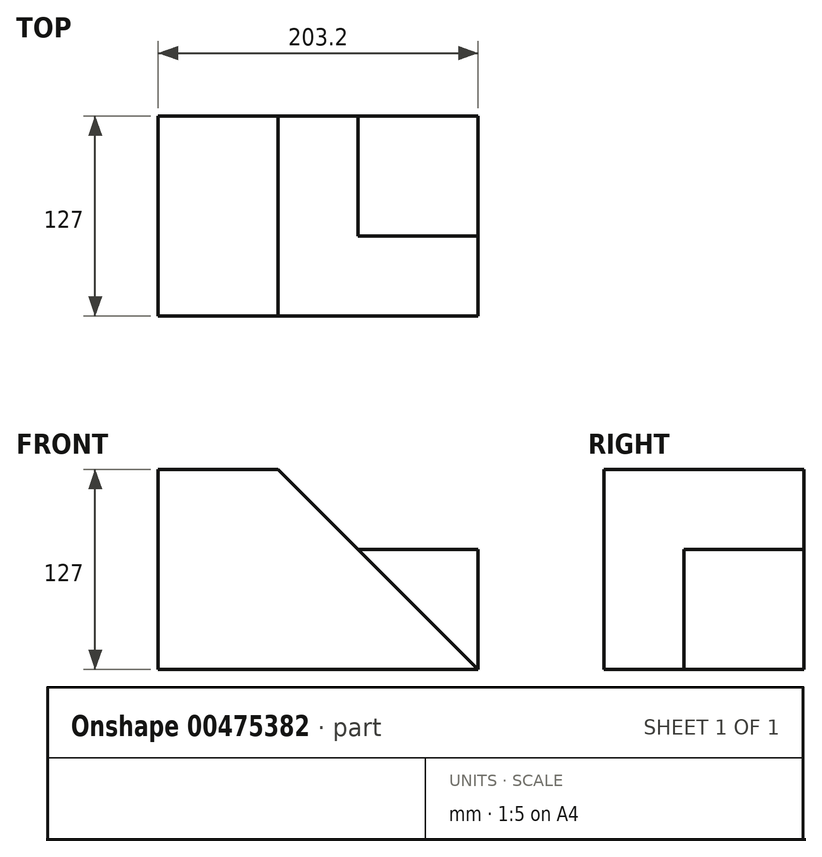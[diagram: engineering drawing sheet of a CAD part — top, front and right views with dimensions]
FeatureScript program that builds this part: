
annotation { "Feature Type Name" : "Feature", "Feature Type Description" : "" }
export const myFeature = defineFeature(function(context is Context, id is Id, definition is map)
    precondition{}
    {
        {
            var Q0;
            Q0=qCreatedBy(makeId("Front.planeOp"),FACE);
            var sketch = newSketch(context, id + "F0", { "sketchPlane" : qUnion([Q0])});
            skLineSegment(sketch, "E0.bottom", {"start": v(0, 0) * mm, "end": v(203.2, 0) * mm});
            skLineSegment(sketch, "E0.top", {"start": v(0, 127) * mm, "end": v(203.2, 127) * mm});
            skLineSegment(sketch, "E0.left", {"start": v(0, 0) * mm, "end": v(0, 127) * mm});
            skLineSegment(sketch, "E0.right", {"start": v(203.2, 0) * mm, "end": v(203.2, 127) * mm});
            skLineSegment(sketch, "E1", {"start": v(203.2, 0) * mm, "end": v(76.2, 127) * mm});
            skLineSegment(sketch, "E2", {"start": v(203.2, 76.2) * mm, "end": v(127, 76.2) * mm});
            skSolve(sketch);
        }
        {
            var Q0;
            {var subQ2=sQuery(id+"F0.wireOp",EDGE,"E0.bottom");Q0=makeQuery(id+"F0.imprint","IMPRINT",FACE,{"disambiguationData":[TD([[makeQuery(id+"F0.imprint","IMPRINT",EDGE,{"derivedFrom":subQ2}),1.0]])]});}
            extrude(context, id + "F1", {"entities" : qUnion([Q0]), "depth" : 127 * mm, "offsetDistance" : 25.4 * mm});
        }
        {
            var Q0;
            {var subQ3=sQuery(id+"F0.wireOp",EDGE,"E2");Q0=makeQuery(id+"F0.imprint","IMPRINT",FACE,{"disambiguationData":[TD([[makeQuery(id+"F0.imprint","IMPRINT",EDGE,{"derivedFrom":subQ3}),1.0]])]});}
            extrude(context, id + "F2", {"entities" : qUnion([Q0]), "operationType" : NewBodyOperationType.ADD, "depth" : 76.2 * mm, "offsetDistance" : 25.4 * mm});
        }
    });
